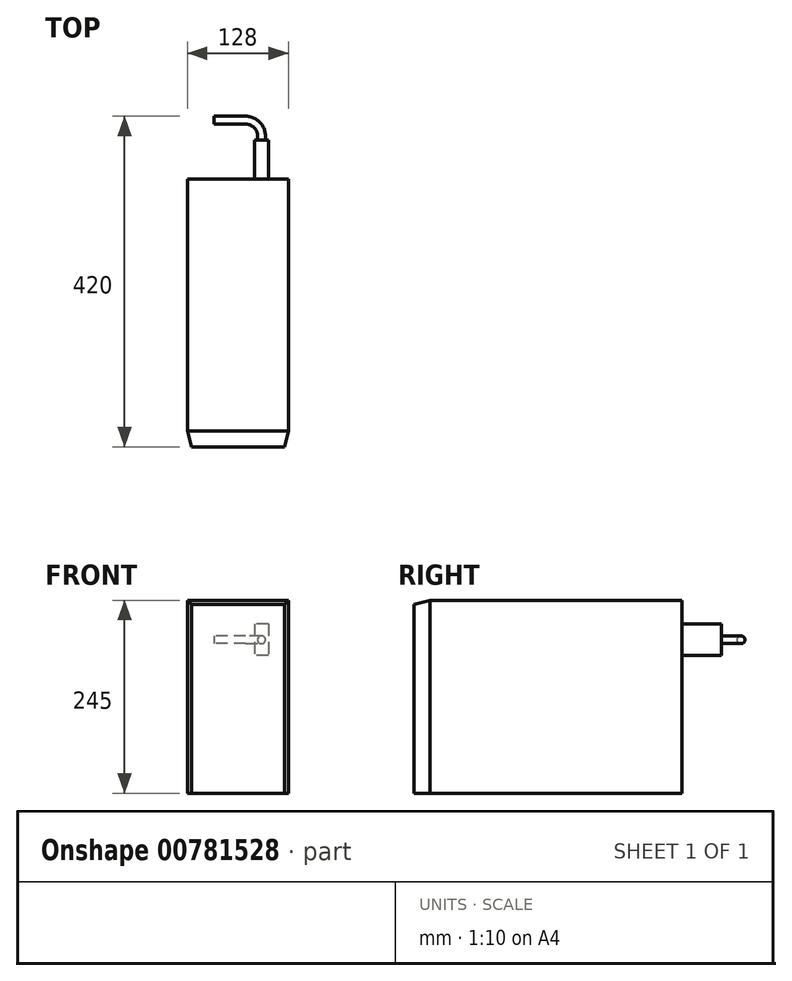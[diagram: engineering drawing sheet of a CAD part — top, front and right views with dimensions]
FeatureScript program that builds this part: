
annotation { "Feature Type Name" : "Feature", "Feature Type Description" : "" }
export const myFeature = defineFeature(function(context is Context, id is Id, definition is map)
    precondition{}
    {
        {
            var Q0;
            Q0=qCreatedBy(makeId("Top.planeOp"),FACE);
            var sketch = newSketch(context, id + "F0", { "sketchPlane" : qUnion([Q0])});
            skLineSegment(sketch, "E0.bottom", {"start": v(0, 0) * mm, "end": v(128, 0) * mm});
            skLineSegment(sketch, "E0.top", {"start": v(0, 340) * mm, "end": v(128, 340) * mm});
            skLineSegment(sketch, "E0.left", {"start": v(0, 0) * mm, "end": v(0, 340) * mm});
            skLineSegment(sketch, "E0.right", {"start": v(128, 0) * mm, "end": v(128, 340) * mm});
            skSolve(sketch);
        }
        {
            var Q0;
            Q0 = qSketchRegion(id + "F0", true);
            extrude(context, id + "F1", {"entities" : qUnion([Q0]), "depth" : 245 * mm, "offsetDistance" : 25 * mm});
        }
        {
            var Q0;
            Q0=makeQuery(id+"F1.opExtrude","SWEPT_EDGE",EDGE,{"disambiguationData":[OSD([sQuery(id+"F0.wireOp",EDGE,"E0.bottom"),sQuery(id+"F0.wireOp",EDGE,"E0.right")])]});
            var Q1;
            Q1=makeQuery(id+"F1.opExtrude","SWEPT_EDGE",EDGE,{"disambiguationData":[OSD([sQuery(id+"F0.wireOp",EDGE,"E0.bottom"),sQuery(id+"F0.wireOp",EDGE,"E0.left")])]});
            var Q2;
            Q2=makeQuery(id+"F1.opExtrude","CAP_EDGE",EDGE,{"disambiguationData":[OSD([sQuery(id+"F0.wireOp",EDGE,"E0.bottom")])],"isStart":false});
            chamfer(context, id + "F2", {"entities" : qUnion([Q0, Q1, Q2]), "chamferType" : ChamferType.TWO_OFFSETS, "width1" : 20 * mm, "oppositeDirection" : false, "width2" : 5 * mm, "tangentPropagation" : true});
        }
        {
            var Q0;
            Q0=makeQuery(id+"F1.opExtrude","SWEPT_FACE",FACE,{"disambiguationData":[OSD([sQuery(id+"F0.wireOp",EDGE,"E0.top")])]});
            var sketch = newSketch(context, id + "F3", { "sketchPlane" : qUnion([Q0])});
            skLineSegment(sketch, "E1.bottom", {"start": v(-103, 215) * mm, "end": v(-85, 215) * mm});
            skLineSegment(sketch, "E1.top", {"start": v(-103, 175) * mm, "end": v(-85, 175) * mm});
            skLineSegment(sketch, "E1.left", {"start": v(-103, 215) * mm, "end": v(-103, 175) * mm});
            skLineSegment(sketch, "E1.right", {"start": v(-85, 215) * mm, "end": v(-85, 175) * mm});
            skSolve(sketch);
        }
        {
            var Q0;
            Q0 = qSketchRegion(id + "F3", true);
            extrude(context, id + "F4", {"entities" : qUnion([Q0]), "operationType" : NewBodyOperationType.ADD, "depth" : 50 * mm, "offsetDistance" : 25 * mm});
        }
        {
            var Q0;
            Q0=makeQuery(id+"F4.opExtrude","SWEPT_FACE",FACE,{"disambiguationData":[OSD([sQuery(id+"F3.wireOp",EDGE,"E1.bottom")])]});
            var Q1;
            Q1=makeQuery(id+"F4.opExtrude","SWEPT_FACE",FACE,{"disambiguationData":[OSD([sQuery(id+"F3.wireOp",EDGE,"E1.top")])]});
            cPlane(context, id + "F5", {"entities" : qUnion([Q0, Q1]), "cplaneType" : CPlaneType.MID_PLANE, "offset" : 25 * mm, "width" : 150 * mm, "height" : 150 * mm});
        }
        {
            var Q0;
            Q0=qCreatedBy(id+"F5.planeOp",FACE);
            var sketch = newSketch(context, id + "F6", { "sketchPlane" : qUnion([Q0])});
            skLineSegment(sketch, "E2", {"start": v(94, 390) * mm, "end": v(94, 395) * mm});
            skPoint(sketch, "E3.visualSharp", {"position": v(94, 415) * mm});
            skLineSegment(sketch, "E4", {"start": v(74, 415) * mm, "end": v(34, 415) * mm});
            skArc(sketch, "E5.filletArc", {"start": v(94, 395) * mm, "mid": v(88.14, 409.14) * mm, "end": v(74, 415) * mm});
            skSolve(sketch);
        }
        {
            var Q0;
            Q0=makeQuery(id+"F4.opExtrude","CAP_FACE",FACE,{"disambiguationData":[OSD([sQuery(id+"F3.wireOp",EDGE,"E1.bottom"),sQuery(id+"F3.wireOp",EDGE,"E1.top"),sQuery(id+"F3.wireOp",EDGE,"E1.left"),sQuery(id+"F3.wireOp",EDGE,"E1.right")])],"isStart":false});
            var sketch = newSketch(context, id + "F7", { "sketchPlane" : qUnion([Q0])});
            skCircle(sketch, "E6", {"center": v(-94, 195) * mm, "radius": 5 * mm});
            skPoint(sketch, "E6.centerSnap0", {"position": v(-94, 215) * mm});
            skSolve(sketch);
        }
        {
            var Q0;
            Q0=makeQuery(id+"F7.imprint","IMPRINT",FACE,{"disambiguationData":[TD([[makeQuery(id+"F7.imprint","IMPRINT",EDGE,{"derivedFrom":sQuery(id+"F7.wireOp",EDGE,"E6")}),1.0]])]});
            var Q1;
            Q1=sQuery(id+"F6.wireOp",EDGE,"E2");
            var Q2;
            Q2=sQuery(id+"F6.wireOp",EDGE,"E5.filletArc");
            var Q3;
            Q3=sQuery(id+"F6.wireOp",EDGE,"E4");
            sweep(context, id + "F8", {"operationType" : NewBodyOperationType.ADD, "profiles" : qUnion([Q0]), "path" : qUnion([Q1, Q2, Q3])});
        }
    });
